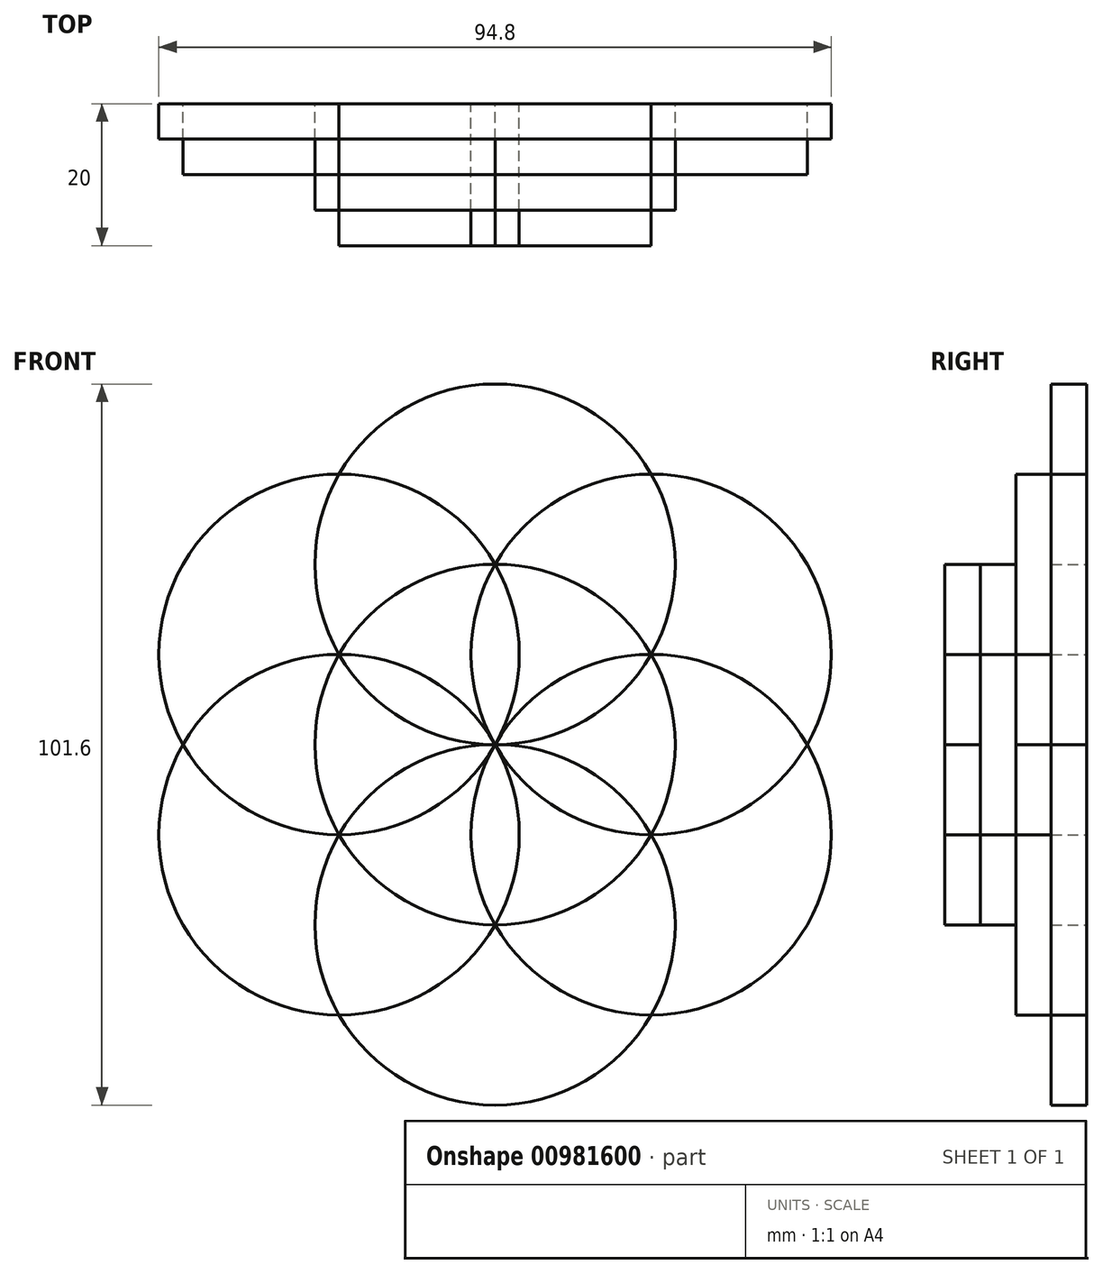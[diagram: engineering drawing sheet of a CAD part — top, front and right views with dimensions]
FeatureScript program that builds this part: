
annotation { "Feature Type Name" : "Feature", "Feature Type Description" : "" }
export const myFeature = defineFeature(function(context is Context, id is Id, definition is map)
    precondition{}
    {
        {
            var Q0;
            Q0=qCreatedBy(makeId("Front.planeOp"),FACE);
            var sketch = newSketch(context, id + "F0", { "sketchPlane" : qUnion([Q0])});
            skCircle(sketch, "E0", {"center": v(0, 0) * mm, "radius": 25.4 * mm});
            skCircle(sketch, "E1", {"center": v(0, 25.4) * mm, "radius": 25.4 * mm});
            skCircle(sketch, "E2", {"center": v(22, 12.7) * mm, "radius": 25.4 * mm});
            skCircle(sketch, "E3", {"center": v(22, -12.7) * mm, "radius": 25.4 * mm});
            skCircle(sketch, "E4", {"center": v(0, -25.4) * mm, "radius": 25.4 * mm});
            skCircle(sketch, "E5", {"center": v(-22, -12.7) * mm, "radius": 25.4 * mm});
            skCircle(sketch, "E6", {"center": v(-22, 12.7) * mm, "radius": 25.4 * mm});
            skSolve(sketch);
        }
        {
            var Q0;
            {var subQ0=sQuery(id+"F0.wireOp",EDGE,"E5");var subQ1=sQuery(id+"F0.wireOp",EDGE,"E1");var subQ2=makeQuery(id+"F0.imprint","INTERSECT",VERTEX,{"derivedFrom":[sQuery(id+"F0.wireOp",EDGE,"E0"),subQ1,subQ0]});Q0=makeQuery(id+"F0.imprint","IMPRINT",FACE,{"disambiguationData":[TD([[makeQuery(id+"F0.imprint","IMPRINT",EDGE,{"disambiguationData":[TD([[subQ2,-1.0]])],"derivedFrom":subQ1}),1.0]])]});}
            var Q1;
            {var subQ0=sQuery(id+"F0.wireOp",EDGE,"E6");var subQ1=sQuery(id+"F0.wireOp",EDGE,"E2");var subQ2=makeQuery(id+"F0.imprint","INTERSECT",VERTEX,{"derivedFrom":[sQuery(id+"F0.wireOp",EDGE,"E0"),subQ1,subQ0]});Q1=makeQuery(id+"F0.imprint","IMPRINT",FACE,{"disambiguationData":[TD([[makeQuery(id+"F0.imprint","IMPRINT",EDGE,{"disambiguationData":[TD([[subQ2,-1.0]])],"derivedFrom":subQ1}),1.0]])]});}
            var Q2;
            {var subQ0=sQuery(id+"F0.wireOp",EDGE,"E3");var subQ1=sQuery(id+"F0.wireOp",EDGE,"E1");var subQ2=makeQuery(id+"F0.imprint","INTERSECT",VERTEX,{"derivedFrom":[sQuery(id+"F0.wireOp",EDGE,"E0"),subQ1,subQ0]});Q2=makeQuery(id+"F0.imprint","IMPRINT",FACE,{"disambiguationData":[TD([[makeQuery(id+"F0.imprint","IMPRINT",EDGE,{"disambiguationData":[TD([[subQ2,1.0]])],"derivedFrom":subQ1}),1.0]])]});}
            var Q3;
            {var subQ0=sQuery(id+"F0.wireOp",EDGE,"E4");var subQ1=sQuery(id+"F0.wireOp",EDGE,"E2");var subQ2=makeQuery(id+"F0.imprint","INTERSECT",VERTEX,{"derivedFrom":[sQuery(id+"F0.wireOp",EDGE,"E0"),subQ1,subQ0]});Q3=makeQuery(id+"F0.imprint","IMPRINT",FACE,{"disambiguationData":[TD([[makeQuery(id+"F0.imprint","IMPRINT",EDGE,{"disambiguationData":[TD([[subQ2,1.0]])],"derivedFrom":subQ1}),1.0]])]});}
            var Q4;
            {var subQ0=sQuery(id+"F0.wireOp",EDGE,"E5");var subQ1=sQuery(id+"F0.wireOp",EDGE,"E3");var subQ2=makeQuery(id+"F0.imprint","INTERSECT",VERTEX,{"derivedFrom":[sQuery(id+"F0.wireOp",EDGE,"E0"),subQ1,subQ0]});Q4=makeQuery(id+"F0.imprint","IMPRINT",FACE,{"disambiguationData":[TD([[makeQuery(id+"F0.imprint","IMPRINT",EDGE,{"disambiguationData":[TD([[subQ2,1.0]])],"derivedFrom":subQ1}),1.0]])]});}
            var Q5;
            {var subQ0=sQuery(id+"F0.wireOp",EDGE,"E6");var subQ1=sQuery(id+"F0.wireOp",EDGE,"E4");var subQ2=makeQuery(id+"F0.imprint","INTERSECT",VERTEX,{"derivedFrom":[sQuery(id+"F0.wireOp",EDGE,"E0"),subQ1,subQ0]});Q5=makeQuery(id+"F0.imprint","IMPRINT",FACE,{"disambiguationData":[TD([[makeQuery(id+"F0.imprint","IMPRINT",EDGE,{"disambiguationData":[TD([[subQ2,1.0]])],"derivedFrom":subQ1}),1.0]])]});}
            extrude(context, id + "F1", {"entities" : qUnion([Q0, Q1, Q2, Q3, Q4, Q5]), "depth" : 20 * mm, "offsetDistance" : 25.4 * mm});
        }
        {
            var Q0;
            {var subQ0=sQuery(id+"F0.wireOp",EDGE,"E6");var subQ1=sQuery(id+"F0.wireOp",EDGE,"E2");var subQ2=sQuery(id+"F0.wireOp",EDGE,"E0");var subQ3=makeQuery(id+"F0.imprint","INTERSECT",VERTEX,{"derivedFrom":[subQ2,subQ1,subQ0]});Q0=makeQuery(id+"F0.imprint","IMPRINT",FACE,{"disambiguationData":[TD([[makeQuery(id+"F0.imprint","IMPRINT",EDGE,{"disambiguationData":[TD([[subQ3,-1.0]])],"derivedFrom":subQ2}),1.0]])]});}
            var Q1;
            {var subQ0=sQuery(id+"F0.wireOp",EDGE,"E6");var subQ1=sQuery(id+"F0.wireOp",EDGE,"E2");var subQ2=sQuery(id+"F0.wireOp",EDGE,"E0");var subQ3=makeQuery(id+"F0.imprint","INTERSECT",VERTEX,{"derivedFrom":[subQ2,subQ1,subQ0]});Q1=makeQuery(id+"F0.imprint","IMPRINT",FACE,{"disambiguationData":[TD([[makeQuery(id+"F0.imprint","IMPRINT",EDGE,{"disambiguationData":[TD([[subQ3,1.0]])],"derivedFrom":subQ2}),1.0]])]});}
            var Q2;
            {var subQ0=sQuery(id+"F0.wireOp",EDGE,"E3");var subQ1=sQuery(id+"F0.wireOp",EDGE,"E1");var subQ2=sQuery(id+"F0.wireOp",EDGE,"E0");var subQ3=makeQuery(id+"F0.imprint","INTERSECT",VERTEX,{"derivedFrom":[subQ2,subQ1,subQ0]});Q2=makeQuery(id+"F0.imprint","IMPRINT",FACE,{"disambiguationData":[TD([[makeQuery(id+"F0.imprint","IMPRINT",EDGE,{"disambiguationData":[TD([[subQ3,1.0]])],"derivedFrom":subQ2}),1.0]])]});}
            var Q3;
            {var subQ0=sQuery(id+"F0.wireOp",EDGE,"E5");var subQ1=sQuery(id+"F0.wireOp",EDGE,"E3");var subQ2=sQuery(id+"F0.wireOp",EDGE,"E0");var subQ3=makeQuery(id+"F0.imprint","INTERSECT",VERTEX,{"derivedFrom":[subQ2,subQ1,subQ0]});Q3=makeQuery(id+"F0.imprint","IMPRINT",FACE,{"disambiguationData":[TD([[makeQuery(id+"F0.imprint","IMPRINT",EDGE,{"disambiguationData":[TD([[subQ3,-1.0]])],"derivedFrom":subQ2}),1.0]])]});}
            var Q4;
            {var subQ0=sQuery(id+"F0.wireOp",EDGE,"E6");var subQ1=sQuery(id+"F0.wireOp",EDGE,"E4");var subQ2=sQuery(id+"F0.wireOp",EDGE,"E0");var subQ3=makeQuery(id+"F0.imprint","INTERSECT",VERTEX,{"derivedFrom":[subQ2,subQ1,subQ0]});Q4=makeQuery(id+"F0.imprint","IMPRINT",FACE,{"disambiguationData":[TD([[makeQuery(id+"F0.imprint","IMPRINT",EDGE,{"disambiguationData":[TD([[subQ3,-1.0]])],"derivedFrom":subQ2}),1.0]])]});}
            var Q5;
            {var subQ0=sQuery(id+"F0.wireOp",EDGE,"E5");var subQ1=sQuery(id+"F0.wireOp",EDGE,"E1");var subQ2=sQuery(id+"F0.wireOp",EDGE,"E0");var subQ3=makeQuery(id+"F0.imprint","INTERSECT",VERTEX,{"derivedFrom":[subQ2,subQ1,subQ0]});Q5=makeQuery(id+"F0.imprint","IMPRINT",FACE,{"disambiguationData":[TD([[makeQuery(id+"F0.imprint","IMPRINT",EDGE,{"disambiguationData":[TD([[subQ3,-1.0]])],"derivedFrom":subQ2}),1.0]])]});}
            extrude(context, id + "F2", {"entities" : qUnion([Q0, Q1, Q2, Q3, Q4, Q5]), "depth" : 15 * mm, "offsetDistance" : 25 * mm});
        }
        {
            var Q0;
            {var subQ0=sQuery(id+"F0.wireOp",EDGE,"E6");var subQ3=sQuery(id+"F0.wireOp",EDGE,"E1");var subQ5=makeQuery(id+"F0.imprint","INTERSECT",VERTEX,{"derivedFrom":[subQ3,subQ0]});Q0=makeQuery(id+"F0.imprint","IMPRINT",FACE,{"disambiguationData":[TD([[makeQuery(id+"F0.imprint","IMPRINT",EDGE,{"disambiguationData":[TD([[subQ5,-1.0]])],"derivedFrom":subQ3}),1.0]])]});}
            var Q1;
            {var subQ0=sQuery(id+"F0.wireOp",EDGE,"E2");var subQ3=sQuery(id+"F0.wireOp",EDGE,"E1");var subQ5=makeQuery(id+"F0.imprint","INTERSECT",VERTEX,{"derivedFrom":[subQ3,subQ0]});Q1=makeQuery(id+"F0.imprint","IMPRINT",FACE,{"disambiguationData":[TD([[makeQuery(id+"F0.imprint","IMPRINT",EDGE,{"disambiguationData":[TD([[subQ5,1.0]])],"derivedFrom":subQ3}),1.0]])]});}
            var Q2;
            {var subQ0=sQuery(id+"F0.wireOp",EDGE,"E3");var subQ3=sQuery(id+"F0.wireOp",EDGE,"E2");var subQ5=makeQuery(id+"F0.imprint","INTERSECT",VERTEX,{"derivedFrom":[subQ3,subQ0]});Q2=makeQuery(id+"F0.imprint","IMPRINT",FACE,{"disambiguationData":[TD([[makeQuery(id+"F0.imprint","IMPRINT",EDGE,{"disambiguationData":[TD([[subQ5,1.0]])],"derivedFrom":subQ3}),1.0]])]});}
            var Q3;
            {var subQ0=sQuery(id+"F0.wireOp",EDGE,"E3");var subQ3=sQuery(id+"F0.wireOp",EDGE,"E4");var subQ5=makeQuery(id+"F0.imprint","INTERSECT",VERTEX,{"derivedFrom":[subQ0,subQ3]});Q3=makeQuery(id+"F0.imprint","IMPRINT",FACE,{"disambiguationData":[TD([[makeQuery(id+"F0.imprint","IMPRINT",EDGE,{"disambiguationData":[TD([[subQ5,1.0]])],"derivedFrom":subQ0}),1.0]])]});}
            var Q4;
            {var subQ0=sQuery(id+"F0.wireOp",EDGE,"E4");var subQ3=sQuery(id+"F0.wireOp",EDGE,"E5");var subQ5=makeQuery(id+"F0.imprint","INTERSECT",VERTEX,{"derivedFrom":[subQ0,subQ3]});Q4=makeQuery(id+"F0.imprint","IMPRINT",FACE,{"disambiguationData":[TD([[makeQuery(id+"F0.imprint","IMPRINT",EDGE,{"disambiguationData":[TD([[subQ5,1.0]])],"derivedFrom":subQ0}),1.0]])]});}
            var Q5;
            {var subQ0=sQuery(id+"F0.wireOp",EDGE,"E5");var subQ3=sQuery(id+"F0.wireOp",EDGE,"E6");var subQ5=makeQuery(id+"F0.imprint","INTERSECT",VERTEX,{"derivedFrom":[subQ0,subQ3]});Q5=makeQuery(id+"F0.imprint","IMPRINT",FACE,{"disambiguationData":[TD([[makeQuery(id+"F0.imprint","IMPRINT",EDGE,{"disambiguationData":[TD([[subQ5,1.0]])],"derivedFrom":subQ0}),1.0]])]});}
            extrude(context, id + "F3", {"entities" : qUnion([Q0, Q1, Q2, Q3, Q4, Q5]), "depth" : 10 * mm, "offsetDistance" : 25 * mm});
        }
        {
            var Q0;
            {var subQ0=sQuery(id+"F0.wireOp",EDGE,"E6");var subQ1=sQuery(id+"F0.wireOp",EDGE,"E1");var subQ2=makeQuery(id+"F0.imprint","INTERSECT",VERTEX,{"derivedFrom":[subQ1,subQ0]});Q0=makeQuery(id+"F0.imprint","IMPRINT",FACE,{"disambiguationData":[TD([[makeQuery(id+"F0.imprint","IMPRINT",EDGE,{"disambiguationData":[TD([[subQ2,-1.0]])],"derivedFrom":subQ0}),1.0]])]});}
            var Q1;
            {var subQ0=sQuery(id+"F0.wireOp",EDGE,"E6");var subQ1=sQuery(id+"F0.wireOp",EDGE,"E1");var subQ2=makeQuery(id+"F0.imprint","INTERSECT",VERTEX,{"derivedFrom":[subQ1,subQ0]});Q1=makeQuery(id+"F0.imprint","IMPRINT",FACE,{"disambiguationData":[TD([[makeQuery(id+"F0.imprint","IMPRINT",EDGE,{"disambiguationData":[TD([[subQ2,1.0]])],"derivedFrom":subQ1}),1.0]])]});}
            var Q2;
            {var subQ0=sQuery(id+"F0.wireOp",EDGE,"E2");var subQ1=sQuery(id+"F0.wireOp",EDGE,"E1");var subQ2=makeQuery(id+"F0.imprint","INTERSECT",VERTEX,{"derivedFrom":[subQ1,subQ0]});Q2=makeQuery(id+"F0.imprint","IMPRINT",FACE,{"disambiguationData":[TD([[makeQuery(id+"F0.imprint","IMPRINT",EDGE,{"disambiguationData":[TD([[subQ2,1.0]])],"derivedFrom":subQ0}),1.0]])]});}
            var Q3;
            {var subQ0=sQuery(id+"F0.wireOp",EDGE,"E3");var subQ1=sQuery(id+"F0.wireOp",EDGE,"E2");var subQ2=makeQuery(id+"F0.imprint","INTERSECT",VERTEX,{"derivedFrom":[subQ1,subQ0]});Q3=makeQuery(id+"F0.imprint","IMPRINT",FACE,{"disambiguationData":[TD([[makeQuery(id+"F0.imprint","IMPRINT",EDGE,{"disambiguationData":[TD([[subQ2,1.0]])],"derivedFrom":subQ0}),1.0]])]});}
            var Q4;
            {var subQ0=sQuery(id+"F0.wireOp",EDGE,"E4");var subQ1=sQuery(id+"F0.wireOp",EDGE,"E3");var subQ2=makeQuery(id+"F0.imprint","INTERSECT",VERTEX,{"derivedFrom":[subQ1,subQ0]});Q4=makeQuery(id+"F0.imprint","IMPRINT",FACE,{"disambiguationData":[TD([[makeQuery(id+"F0.imprint","IMPRINT",EDGE,{"disambiguationData":[TD([[subQ2,1.0]])],"derivedFrom":subQ0}),1.0]])]});}
            var Q5;
            {var subQ0=sQuery(id+"F0.wireOp",EDGE,"E5");var subQ1=sQuery(id+"F0.wireOp",EDGE,"E4");var subQ2=makeQuery(id+"F0.imprint","INTERSECT",VERTEX,{"derivedFrom":[subQ1,subQ0]});Q5=makeQuery(id+"F0.imprint","IMPRINT",FACE,{"disambiguationData":[TD([[makeQuery(id+"F0.imprint","IMPRINT",EDGE,{"disambiguationData":[TD([[subQ2,1.0]])],"derivedFrom":subQ0}),1.0]])]});}
            extrude(context, id + "F4", {"entities" : qUnion([Q0, Q1, Q2, Q3, Q4, Q5]), "depth" : 5 * mm, "offsetDistance" : 25 * mm});
        }
    });
